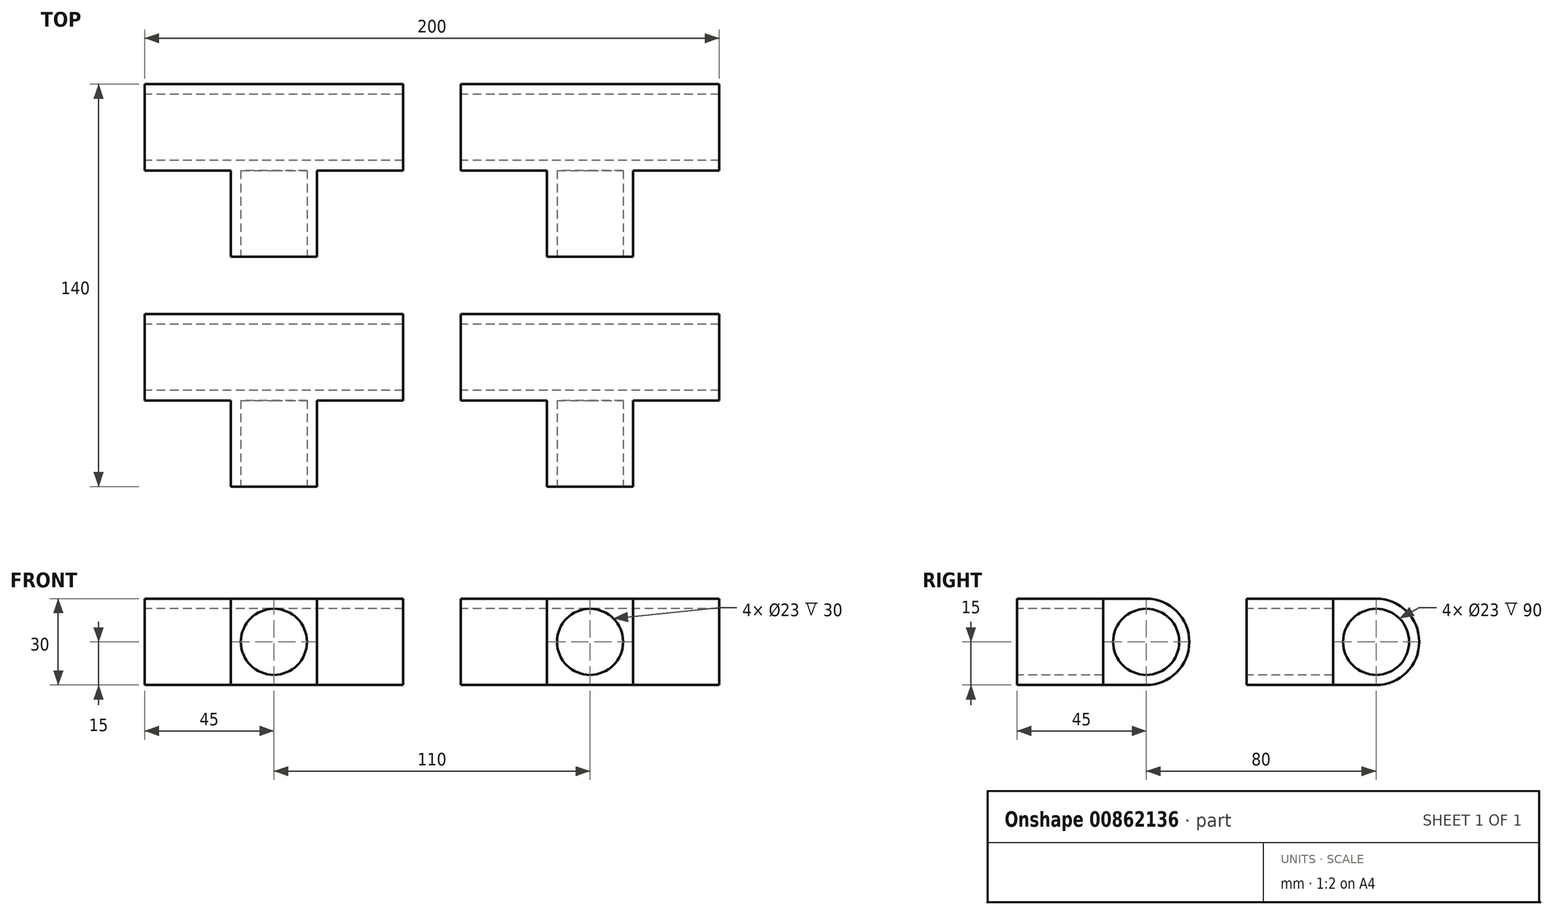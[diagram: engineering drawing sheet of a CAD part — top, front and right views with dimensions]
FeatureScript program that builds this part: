
annotation { "Feature Type Name" : "Feature", "Feature Type Description" : "" }
export const myFeature = defineFeature(function(context is Context, id is Id, definition is map)
    precondition{}
    {
        {
            var Q0;
            Q0=qCreatedBy(makeId("Top.planeOp"),FACE);
            var sketch = newSketch(context, id + "F0", { "sketchPlane" : qUnion([Q0])});
            skLineSegment(sketch, "E0.bottom", {"start": v(45, -15) * mm, "end": v(-45, -15) * mm});
            skLineSegment(sketch, "E0.top", {"start": v(45, 15) * mm, "end": v(-45, 15) * mm});
            skLineSegment(sketch, "E0.left", {"start": v(45, -15) * mm, "end": v(45, 15) * mm});
            skLineSegment(sketch, "E0.right", {"start": v(-45, -15) * mm, "end": v(-45, 15) * mm});
            skPoint(sketch, "E0.middle", {"position": v(0, 0) * mm});
            skLineSegment(sketch, "E1", {"start": v(-15, -15) * mm, "end": v(-15, -45) * mm});
            skLineSegment(sketch, "E2", {"start": v(-15, -45) * mm, "end": v(0, -45) * mm});
            skLineSegment(sketch, "E3.MirrorCS", {"start": v(15, -15) * mm, "end": v(15, -45) * mm});
            skLineSegment(sketch, "E4.MirrorCS", {"start": v(15, -45) * mm, "end": v(0, -45) * mm});
            skSolve(sketch);
        }
        {
            var Q0;
            Q0=makeQuery(id+"F0.imprint","IMPRINT",FACE,{"disambiguationData":[TD([[makeQuery(id+"F0.imprint","IMPRINT",EDGE,{"derivedFrom":sQuery(id+"F0.wireOp",EDGE,"E0.top")}),1.0]])]});
            var Q1;
            {var subQ1=sQuery(id+"F0.wireOp",EDGE,"E1");Q1=makeQuery(id+"F0.imprint","IMPRINT",FACE,{"disambiguationData":[TD([[makeQuery(id+"F0.imprint","IMPRINT",EDGE,{"derivedFrom":subQ1}),1.0]])]});}
            extrude(context, id + "F1", {"entities" : qUnion([Q0, Q1]), "depth" : 30 * mm, "offsetDistance" : 25 * mm});
        }
        {
            var Q0;
            Q0=makeQuery(id+"F1.opExtrude","SWEPT_FACE",FACE,{"disambiguationData":[OSD([sQuery(id+"F0.wireOp",EDGE,"E0.right")])]});
            var sketch = newSketch(context, id + "F2", { "sketchPlane" : qUnion([Q0])});
            skCircle(sketch, "E5", {"center": v(0, 15) * mm, "radius": 11.5 * mm});
            skPoint(sketch, "E5.centerSnap0", {"position": v(-15, 15) * mm});
            skPoint(sketch, "E5.centerSnap1", {"position": v(0, 30) * mm});
            skSolve(sketch);
        }
        {
            var Q0;
            Q0=makeQuery(id+"F1.opExtrude","SWEPT_FACE",FACE,{"disambiguationData":[OSD([sQuery(id+"F0.wireOp",EDGE,"E2"),sQuery(id+"F0.wireOp",EDGE,"E4.MirrorCS")])]});
            var sketch = newSketch(context, id + "F3", { "sketchPlane" : qUnion([Q0])});
            skCircle(sketch, "E6", {"center": v(0, 15) * mm, "radius": 11.5 * mm});
            skPoint(sketch, "E6.centerSnap0", {"position": v(-15, 15) * mm});
            skPoint(sketch, "E6.centerSnap1", {"position": v(0, 30) * mm});
            skSolve(sketch);
        }
        {
            var Q0;
            Q0=makeQuery(id+"F3.imprint","IMPRINT",FACE,{"disambiguationData":[TD([[makeQuery(id+"F3.imprint","IMPRINT",EDGE,{"derivedFrom":sQuery(id+"F3.wireOp",EDGE,"E6")}),1.0]])]});
            extrude(context, id + "F4", {"entities" : qUnion([Q0]), "operationType" : NewBodyOperationType.REMOVE, "oppositeDirection" : true, "depth" : 30 * mm, "offsetDistance" : 25 * mm});
        }
        {
            var Q0;
            Q0=makeQuery(id+"F2.imprint","IMPRINT",FACE,{"disambiguationData":[TD([[makeQuery(id+"F2.imprint","IMPRINT",EDGE,{"derivedFrom":sQuery(id+"F2.wireOp",EDGE,"E5")}),1.0]])]});
            extrude(context, id + "F5", {"entities" : qUnion([Q0]), "operationType" : NewBodyOperationType.REMOVE, "oppositeDirection" : true, "depth" : 90 * mm, "offsetDistance" : 25 * mm});
        }
        {
            var Q0;
            Q0=makeQuery(id+"F1.opExtrude","CAP_EDGE",EDGE,{"disambiguationData":[OSD([sQuery(id+"F0.wireOp",EDGE,"E0.top")])],"isStart":true});
            var Q1;
            Q1=makeQuery(id+"F1.opExtrude","CAP_EDGE",EDGE,{"disambiguationData":[OSD([sQuery(id+"F0.wireOp",EDGE,"E0.top")])],"isStart":false});
            fillet(context, id + "F6", {"entities" : qUnion([Q0, Q1]), "radius" : 15 * mm, "tangentPropagation" : true, "allowEdgeOverflow" : false});
        }
        {
            var Q0;
            Q0=makeQuery(id+"F1.opExtrude","SWEPT_BODY",BODY,{"disambiguationData":[OSD([sQuery(id+"F0.wireOp",EDGE,"E0.bottom"),sQuery(id+"F0.wireOp",EDGE,"E0.top"),sQuery(id+"F0.wireOp",EDGE,"E0.left"),sQuery(id+"F0.wireOp",EDGE,"E0.right"),sQuery(id+"F0.wireOp",EDGE,"E1"),sQuery(id+"F0.wireOp",EDGE,"E2"),sQuery(id+"F0.wireOp",EDGE,"E3.MirrorCS"),sQuery(id+"F0.wireOp",EDGE,"E4.MirrorCS")])]});
            transform(context, id + "F7", {"entities" : qUnion([Q0]), "transformType" : TransformType.TRANSLATION_3D, "dx" : 0 * mm, "dy" : 80 * mm, "dz" : 0 * mm, "makeCopy" : true});
        }
        {
            var Q0;
            Q0=makeQuery(id+"F1.opExtrude","SWEPT_BODY",BODY,{"disambiguationData":[OSD([sQuery(id+"F0.wireOp",EDGE,"E0.bottom"),sQuery(id+"F0.wireOp",EDGE,"E0.top"),sQuery(id+"F0.wireOp",EDGE,"E0.left"),sQuery(id+"F0.wireOp",EDGE,"E0.right"),sQuery(id+"F0.wireOp",EDGE,"E1"),sQuery(id+"F0.wireOp",EDGE,"E2"),sQuery(id+"F0.wireOp",EDGE,"E3.MirrorCS"),sQuery(id+"F0.wireOp",EDGE,"E4.MirrorCS")])]});
            transform(context, id + "F8", {"entities" : qUnion([Q0]), "transformType" : TransformType.TRANSLATION_3D, "dx" : 110 * mm, "dy" : 80 * mm, "dz" : 0 * mm, "makeCopy" : true});
        }
        {
            var Q0;
            Q0=makeQuery(id+"F1.opExtrude","SWEPT_BODY",BODY,{"disambiguationData":[OSD([sQuery(id+"F0.wireOp",EDGE,"E0.bottom"),sQuery(id+"F0.wireOp",EDGE,"E0.top"),sQuery(id+"F0.wireOp",EDGE,"E0.left"),sQuery(id+"F0.wireOp",EDGE,"E0.right"),sQuery(id+"F0.wireOp",EDGE,"E1"),sQuery(id+"F0.wireOp",EDGE,"E2"),sQuery(id+"F0.wireOp",EDGE,"E3.MirrorCS"),sQuery(id+"F0.wireOp",EDGE,"E4.MirrorCS")])]});
            transform(context, id + "F9", {"entities" : qUnion([Q0]), "transformType" : TransformType.TRANSLATION_3D, "dx" : 110 * mm, "dy" : 0 * mm, "dz" : 0 * mm, "makeCopy" : true});
        }
    });
